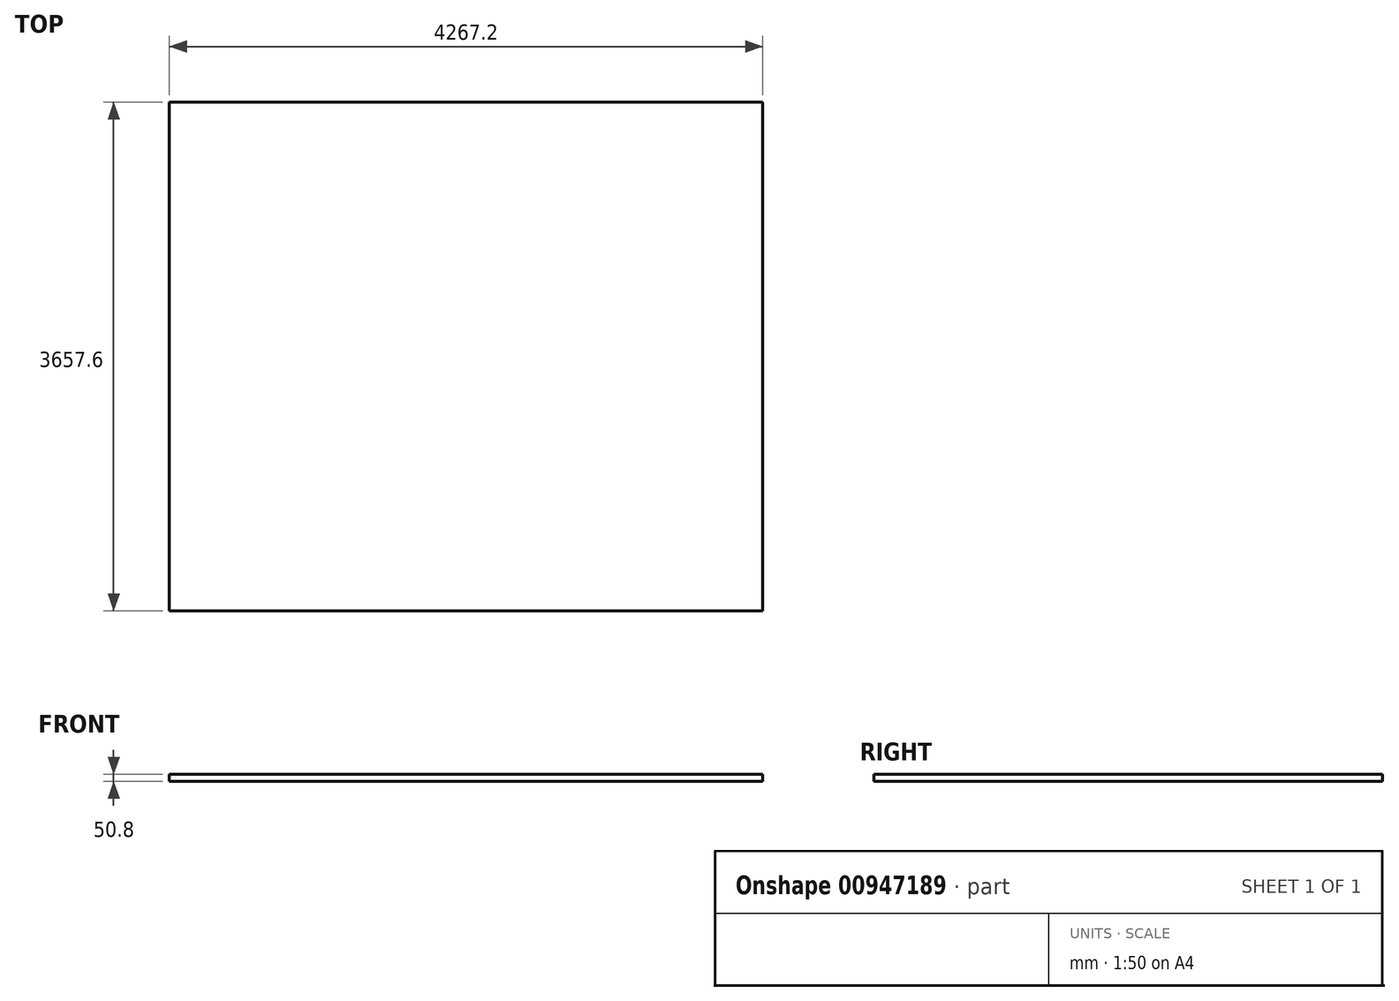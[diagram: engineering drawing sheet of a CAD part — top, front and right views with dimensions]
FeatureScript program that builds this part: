
annotation { "Feature Type Name" : "Feature", "Feature Type Description" : "" }
export const myFeature = defineFeature(function(context is Context, id is Id, definition is map)
    precondition{}
    {
        {
            var Q0;
            Q0=qCreatedBy(makeId("Top.planeOp"),FACE);
            var sketch = newSketch(context, id + "F0", { "sketchPlane" : qUnion([Q0])});
            skLineSegment(sketch, "E0.bottom", {"start": v(0, 0) * mm, "end": v(4267.2, 0) * mm});
            skLineSegment(sketch, "E0.top", {"start": v(0, 3657.6) * mm, "end": v(4267.2, 3657.6) * mm});
            skLineSegment(sketch, "E0.left", {"start": v(0, 0) * mm, "end": v(0, 3657.6) * mm});
            skLineSegment(sketch, "E0.right", {"start": v(4267.2, 0) * mm, "end": v(4267.2, 3657.6) * mm});
            skSolve(sketch);
        }
        {
            var Q0;
            Q0 = qSketchRegion(id + "F0", true);
            extrude(context, id + "F1", {"entities" : qUnion([Q0]), "depth" : 50.8 * mm, "offsetDistance" : 25.4 * mm});
        }
    });
